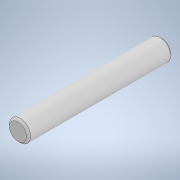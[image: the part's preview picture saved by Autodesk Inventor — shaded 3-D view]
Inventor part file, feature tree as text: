
AUTODESK INVENTOR PART (.ipt)
format: ipt  version: 2022 (Build 260153000, 153)  size: 98,304 bytes
history: native  units: mm
features: extrude x1, chamfer x1, sketch x1
ambient origin geometry x8: Origin, YZ Plane, XZ Plane, XY Plane, X Axis, Y Axis, Z Axis, Center Point
bodies: Solid1 (feature_tree)
feature tree (3):
  extrude  "Extrusion1"  Depth=68.0mm TaperAngle=0.0deg
  chamfer  "Chamfer1"  Distance=1.0mm Angle=45.0deg
  sketch  "Sketch1"  dims[d0=10.0mm d1=68.0mm d2=0.0mm d3=1.0mm d4=2.0mm d5=45.0deg]
